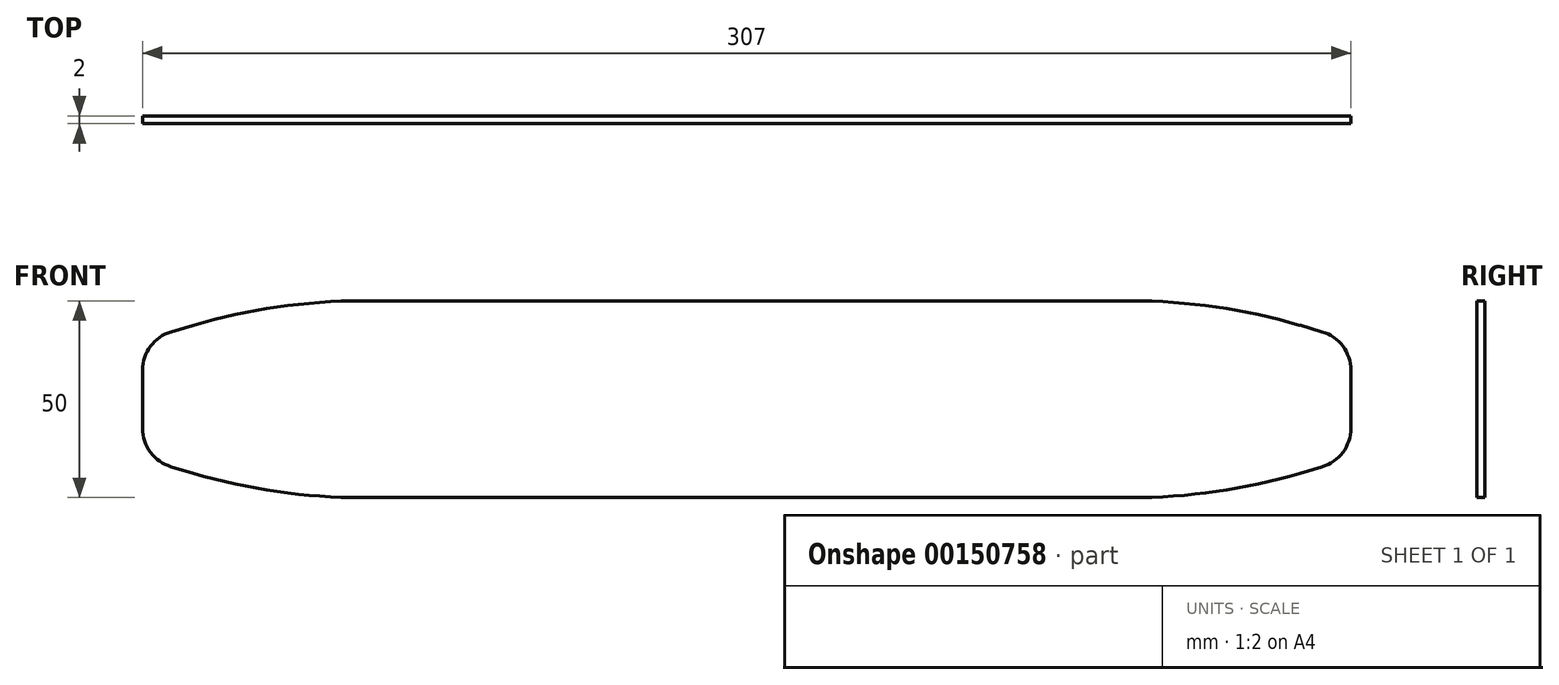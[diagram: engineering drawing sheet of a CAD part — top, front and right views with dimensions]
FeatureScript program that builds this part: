
annotation { "Feature Type Name" : "Feature", "Feature Type Description" : "" }
export const myFeature = defineFeature(function(context is Context, id is Id, definition is map)
    precondition{}
    {
        {
            var Q0;
            Q0=qCreatedBy(makeId("Front.planeOp"),FACE);
            var sketch = newSketch(context, id + "F0", { "sketchPlane" : qUnion([Q0])});
            skLineSegment(sketch, "E0.bottom", {"start": v(-112.15, 0) * mm, "end": v(126.85, 0) * mm});
            skLineSegment(sketch, "E0.top", {"start": v(-112.15, 50) * mm, "end": v(126.85, 50) * mm});
            skLineSegment(sketch, "E1", {"start": v(-112.15, 25) * mm, "end": v(167.89, 25) * mm, "construction": true});
            skPoint(sketch, "E1.endSnap0", {"position": v(-112.15, 25) * mm});
            skLineSegment(sketch, "E2", {"start": v(160.85, 40) * mm, "end": v(160.85, 10) * mm});
            skLineSegment(sketch, "E3", {"start": v(126.85, 50) * mm, "end": v(160.85, 40) * mm});
            skLineSegment(sketch, "E4", {"start": v(126.85, 0) * mm, "end": v(160.85, 10) * mm});
            skLineSegment(sketch, "E5", {"start": v(-146.15, 9.99) * mm, "end": v(-146.15, 39.99) * mm});
            skLineSegment(sketch, "E6", {"start": v(-146.15, 39.99) * mm, "end": v(-112.15, 50) * mm});
            skLineSegment(sketch, "E7", {"start": v(-146.15, 9.99) * mm, "end": v(-112.15, 0) * mm});
            skSolve(sketch);
        }
        {
            var Q0;
            Q0=makeQuery(id+"F0.imprint","IMPRINT",FACE,{"disambiguationData":[TD([[makeQuery(id+"F0.imprint","IMPRINT",EDGE,{"derivedFrom":sQuery(id+"F0.wireOp",EDGE,"E0.bottom")}),1.0]])]});
            extrude(context, id + "F1", {"entities" : qUnion([Q0]), "depth" : 2 * mm});
        }
        {
            var Q0;
            Q0=makeQuery(id+"F1.opExtrude","SWEPT_EDGE",EDGE,{"disambiguationData":[OSD([sQuery(id+"F0.wireOp",EDGE,"E5"),sQuery(id+"F0.wireOp",EDGE,"E6")])]});
            var Q1;
            Q1=makeQuery(id+"F1.opExtrude","SWEPT_EDGE",EDGE,{"disambiguationData":[OSD([sQuery(id+"F0.wireOp",EDGE,"E5"),sQuery(id+"F0.wireOp",EDGE,"E7")])]});
            var Q2;
            Q2=makeQuery(id+"F1.opExtrude","SWEPT_EDGE",EDGE,{"disambiguationData":[OSD([sQuery(id+"F0.wireOp",EDGE,"E2"),sQuery(id+"F0.wireOp",EDGE,"E4")])]});
            var Q3;
            Q3=makeQuery(id+"F1.opExtrude","SWEPT_EDGE",EDGE,{"disambiguationData":[OSD([sQuery(id+"F0.wireOp",EDGE,"E2"),sQuery(id+"F0.wireOp",EDGE,"E3")])]});
            fillet(context, id + "F2", {"entities" : qUnion([Q0, Q1, Q2, Q3]), "radius" : 10.16 * mm, "tangentPropagation" : true, "allowEdgeOverflow" : false});
        }
        {
            var Q0;
            Q0=makeQuery(id+"F1.opExtrude","SWEPT_EDGE",EDGE,{"disambiguationData":[OSD([sQuery(id+"F0.wireOp",EDGE,"E0.top"),sQuery(id+"F0.wireOp",EDGE,"E3")])]});
            var Q1;
            Q1=makeQuery(id+"F1.opExtrude","SWEPT_EDGE",EDGE,{"disambiguationData":[OSD([sQuery(id+"F0.wireOp",EDGE,"E0.bottom"),sQuery(id+"F0.wireOp",EDGE,"E4")])]});
            var Q2;
            Q2=makeQuery(id+"F1.opExtrude","SWEPT_EDGE",EDGE,{"disambiguationData":[OSD([sQuery(id+"F0.wireOp",EDGE,"E0.top"),sQuery(id+"F0.wireOp",EDGE,"E6")])]});
            var Q3;
            Q3=makeQuery(id+"F1.opExtrude","SWEPT_EDGE",EDGE,{"disambiguationData":[OSD([sQuery(id+"F0.wireOp",EDGE,"E0.bottom"),sQuery(id+"F0.wireOp",EDGE,"E7")])]});
            fillet(context, id + "F3", {"entities" : qUnion([Q0, Q1, Q2, Q3]), "radius" : 152.4 * mm, "tangentPropagation" : true, "allowEdgeOverflow" : false});
        }
    });
